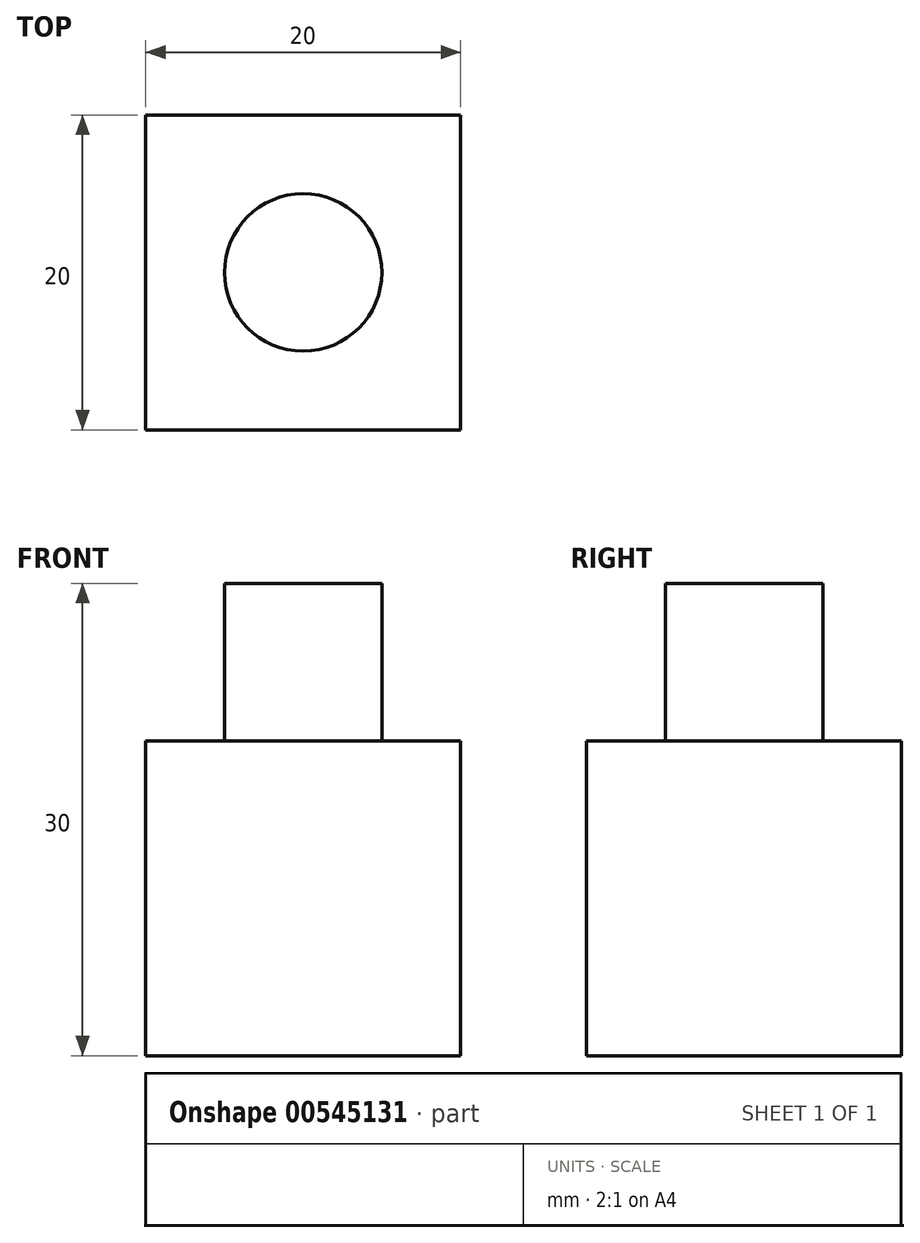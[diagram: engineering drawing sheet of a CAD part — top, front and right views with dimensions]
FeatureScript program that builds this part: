
annotation { "Feature Type Name" : "Feature", "Feature Type Description" : "" }
export const myFeature = defineFeature(function(context is Context, id is Id, definition is map)
    precondition{}
    {
        {
            var Q0;
            Q0=qCreatedBy(makeId("Top.planeOp"),FACE);
            var sketch = newSketch(context, id + "F0", { "sketchPlane" : qUnion([Q0])});
            skLineSegment(sketch, "E0.bottom", {"start": v(0, 0) * mm, "end": v(-20, 0) * mm});
            skLineSegment(sketch, "E0.top", {"start": v(0, 20) * mm, "end": v(-20, 20) * mm});
            skLineSegment(sketch, "E0.left", {"start": v(0, 0) * mm, "end": v(0, 20) * mm});
            skLineSegment(sketch, "E0.right", {"start": v(-20, 0) * mm, "end": v(-20, 20) * mm});
            skSolve(sketch);
        }
        {
            var Q0;
            Q0=makeQuery(id+"F0.imprint","IMPRINT",FACE,{"disambiguationData":[TD([[makeQuery(id+"F0.imprint","IMPRINT",EDGE,{"derivedFrom":sQuery(id+"F0.wireOp",EDGE,"E0.bottom")}),-1.0]])]});
            extrude(context, id + "F1", {"entities" : qUnion([Q0]), "depth" : 20 * mm, "offsetDistance" : 25 * mm});
        }
        {
            var Q0;
            Q0=makeQuery(id+"F1.opExtrude","CAP_FACE",FACE,{"disambiguationData":[OSD([sQuery(id+"F0.wireOp",EDGE,"E0.bottom"),sQuery(id+"F0.wireOp",EDGE,"E0.top"),sQuery(id+"F0.wireOp",EDGE,"E0.left"),sQuery(id+"F0.wireOp",EDGE,"E0.right")])],"isStart":false});
            var sketch = newSketch(context, id + "F2", { "sketchPlane" : qUnion([Q0])});
            skLineSegment(sketch, "E1", {"start": v(-20, 20) * mm, "end": v(0, 0) * mm, "construction": true});
            skLineSegment(sketch, "E2", {"start": v(0, 20) * mm, "end": v(-20, 0) * mm, "construction": true});
            skCircle(sketch, "E3", {"center": v(-10, 10) * mm, "radius": 5 * mm});
            skSolve(sketch);
        }
        {
            var Q0;
            Q0 = qSketchRegion(id + "F2", true);
            extrude(context, id + "F3", {"entities" : qUnion([Q0]), "operationType" : NewBodyOperationType.ADD, "depth" : 10 * mm, "offsetDistance" : 25 * mm});
        }
    });
